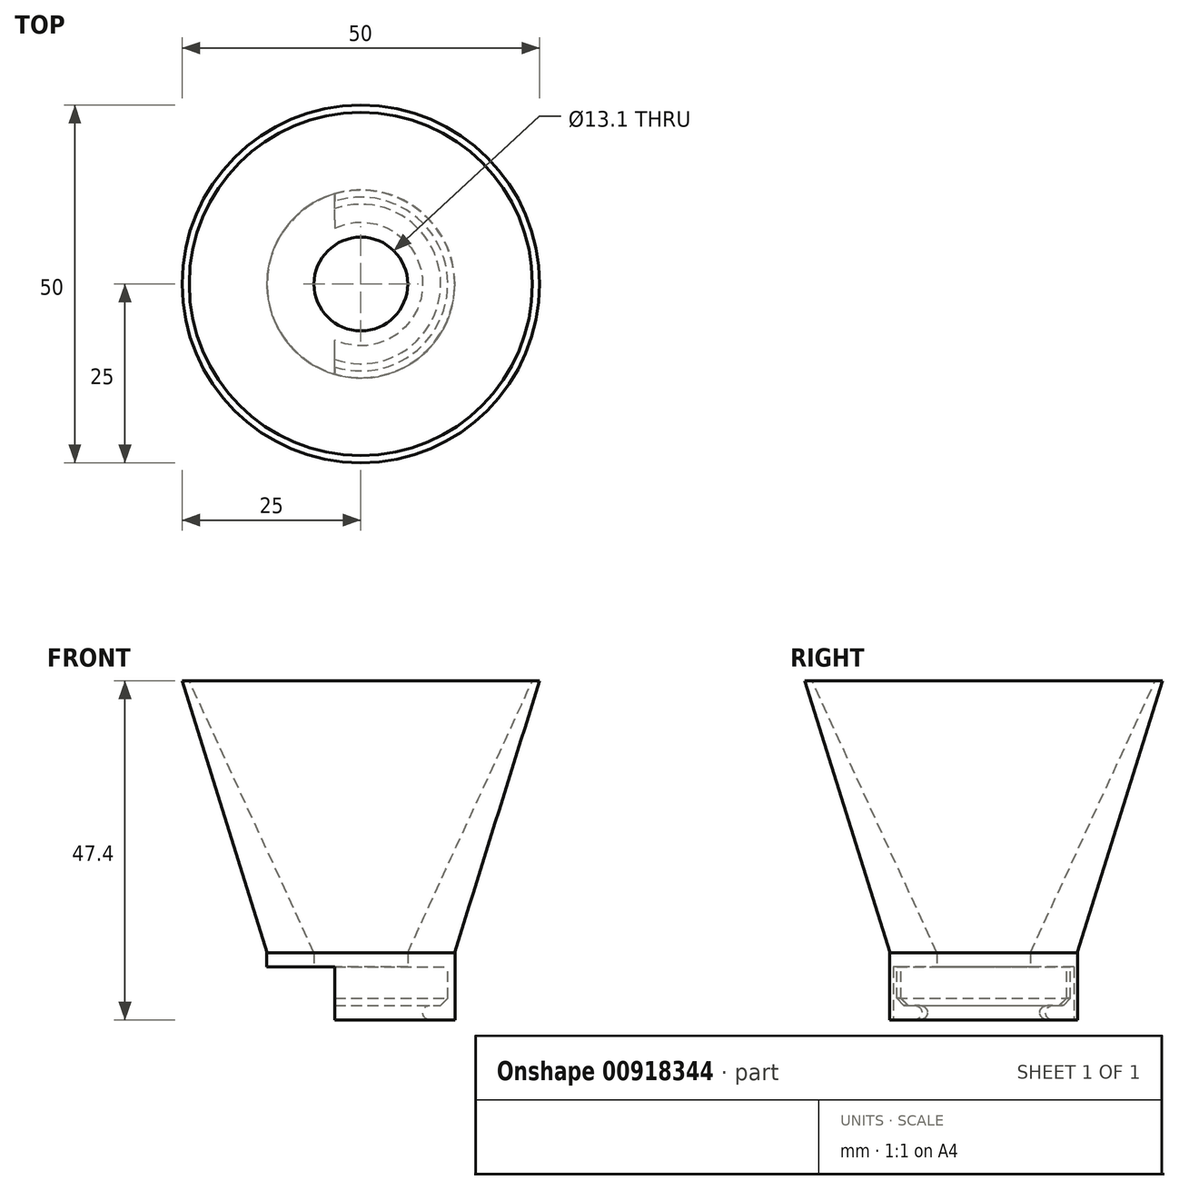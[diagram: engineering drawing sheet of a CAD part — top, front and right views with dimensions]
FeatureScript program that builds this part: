
annotation { "Feature Type Name" : "Feature", "Feature Type Description" : "" }
export const myFeature = defineFeature(function(context is Context, id is Id, definition is map)
    precondition{}
    {
        {
            var Q0;
            Q0=qCreatedBy(makeId("Top.planeOp"),FACE);
            var sketch = newSketch(context, id + "F0", { "sketchPlane" : qUnion([Q0])});
            skCircle(sketch, "E0", {"center": v(0, 0) * mm, "radius": 8.65 * mm});
            skCircle(sketch, "E1.0", {"center": v(0, 0) * mm, "radius": 13.15 * mm});
            skLineSegment(sketch, "E2", {"start": v(-3.65, 15.06) * mm, "end": v(-3.65, -15.06) * mm});
            skSolve(sketch);
        }
        {
            var Q0;
            Q0=qCreatedBy(makeId("Top.planeOp"),FACE);
            cPlane(context, id + "F1", {"entities" : qUnion([Q0]), "cplaneType" : CPlaneType.OFFSET, "offset" : 5.4 * mm, "width" : 150 * mm, "height" : 150 * mm});
        }
        {
            var Q0;
            Q0=makeQuery(id+"F0.imprint","IMPRINT",FACE,{"disambiguationData":[TD([[makeQuery(id+"F0.imprint","IMPRINT",EDGE,{"derivedFrom":sQuery(id+"F0.wireOp",EDGE,"E0")}),-1.0]])]});
            extrude(context, id + "F2", {"entities" : qUnion([Q0]), "oppositeDirection" : true, "depth" : 2 * mm, "offsetDistance" : 25 * mm});
        }
        {
            var Q0;
            Q0=qCreatedBy(id+"F1.planeOp",FACE);
            var sketch = newSketch(context, id + "F3", { "sketchPlane" : qUnion([Q0])});
            skCircle(sketch, "E3", {"center": v(0, 0) * mm, "radius": 6.55 * mm});
            skCircle(sketch, "E4.0", {"center": v(0, 0) * mm, "radius": 12.15 * mm});
            skCircle(sketch, "E5.0", {"center": v(0, 0) * mm, "radius": 13.15 * mm});
            skSolve(sketch);
        }
        {
            var Q0;
            Q0=makeQuery(id+"F3.imprint","IMPRINT",FACE,{"disambiguationData":[TD([[makeQuery(id+"F3.imprint","IMPRINT",EDGE,{"derivedFrom":sQuery(id+"F3.wireOp",EDGE,"E3")}),-1.0]])]});
            extrude(context, id + "F4", {"entities" : qUnion([Q0]), "depth" : 2 * mm, "offsetDistance" : 25 * mm});
        }
        {
            var Q0;
            Q0=makeQuery(id+"F3.imprint","IMPRINT",FACE,{"disambiguationData":[TD([[makeQuery(id+"F3.imprint","IMPRINT",EDGE,{"derivedFrom":sQuery(id+"F3.wireOp",EDGE,"E4.0")}),-1.0]])]});
            extrude(context, id + "F5", {"entities" : qUnion([Q0]), "operationType" : NewBodyOperationType.ADD, "oppositeDirection" : true, "depth" : 6.2 * mm, "offsetDistance" : 25 * mm, "hasSecondDirection" : true, "secondDirectionOppositeDirection" : false, "secondDirectionDepth" : 2 * mm});
        }
        {
            var Q0;
            {var subQ0=sQuery(id+"F0.wireOp",EDGE,"E2");var subQ1=sQuery(id+"F0.wireOp",EDGE,"E0");var subQ2=makeQuery(id+"F0.imprint","INTERSECT",VERTEX,{"disambiguationData":[OD(0.0)],"derivedFrom":[subQ1,subQ0]});Q0=makeQuery(id+"F0.imprint","IMPRINT",FACE,{"disambiguationData":[TD([[makeQuery(id+"F0.imprint","IMPRINT",EDGE,{"disambiguationData":[TD([[subQ2,-1.0]])],"derivedFrom":subQ1}),-1.0]])]});}
            extrude(context, id + "F6", {"entities" : qUnion([Q0]), "operationType" : NewBodyOperationType.REMOVE, "depth" : 5.4 * mm, "offsetDistance" : 25 * mm, "hasSecondDirection" : true, "secondDirectionOppositeDirection" : true, "secondDirectionDepth" : 25 * mm});
        }
        {
            var Q0;
            Q0=makeQuery(id+"F5.boolean.opBoolean","INTERSECT",EDGE,{"derivedFrom":[makeQuery(id+"F2.opExtrude","CAP_FACE",FACE,{"disambiguationData":[OSD([sQuery(id+"F0.wireOp",EDGE,"E0"),sQuery(id+"F0.wireOp",EDGE,"E1.0")])],"isStart":true}),makeQuery(id+"F5.opExtrude","SWEPT_FACE",FACE,{"disambiguationData":[OSD([sQuery(id+"F3.wireOp",EDGE,"E4.0")])]})]});
            chamfer(context, id + "F7", {"entities" : qUnion([Q0]), "width" : 1 * mm, "tangentPropagation" : true});
        }
        {
            var Q0;
            Q0=makeQuery(id+"F2.opExtrude","CAP_EDGE",EDGE,{"disambiguationData":[OSD([sQuery(id+"F0.wireOp",EDGE,"E0")])],"isStart":true});
            var Q1;
            Q1=makeQuery(id+"F2.opExtrude","CAP_EDGE",EDGE,{"disambiguationData":[OSD([sQuery(id+"F0.wireOp",EDGE,"E0")])],"isStart":false});
            fillet(context, id + "F8", {"entities" : qUnion([Q0, Q1]), "radius" : 1 * mm, "tangentPropagation" : true, "allowEdgeOverflow" : false});
        }
        {
            var Q0;
            Q0=qCreatedBy(id+"F1.planeOp",FACE);
            cPlane(context, id + "F9", {"entities" : qUnion([Q0]), "cplaneType" : CPlaneType.OFFSET, "offset" : 40 * mm, "width" : 150 * mm, "height" : 150 * mm});
        }
        {
            var Q0;
            Q0=qCreatedBy(id+"F9.planeOp",FACE);
            var sketch = newSketch(context, id + "F10", { "sketchPlane" : qUnion([Q0])});
            skCircle(sketch, "E6", {"center": v(0, 0) * mm, "radius": 25 * mm});
            skSolve(sketch);
        }
        {
            var Q0;
            {var subQ0=sQuery(id+"F3.wireOp",EDGE,"E4.0");Q0=makeQuery(id+"F5.boolean.opBoolean","MERGE",FACE,{"derivedFrom":[makeQuery(id+"F4.opExtrude","CAP_FACE",FACE,{"disambiguationData":[OSD([sQuery(id+"F3.wireOp",EDGE,"E3"),subQ0])],"isStart":false}),makeQuery(id+"F5.opExtrude","CAP_FACE",FACE,{"disambiguationData":[OSD([subQ0,sQuery(id+"F3.wireOp",EDGE,"E5.0")])],"isStart":true})]});}
            var sketch = newSketch(context, id + "F11", { "sketchPlane" : qUnion([Q0])});
            skCircle(sketch, "E7", {"center": v(0, 0) * mm, "radius": 13.1 * mm});
            skSolve(sketch);
        }
        {
            var Q1;
            Q1 = qSketchRegion(id + "F11", true);
            var Q2;
            Q2=makeQuery(id+"F10.imprint","IMPRINT",FACE,{"disambiguationData":[TD([[makeQuery(id+"F10.imprint","IMPRINT",EDGE,{"derivedFrom":sQuery(id+"F10.wireOp",EDGE,"E6")}),1.0]])]});
            loft(context, id + "F12", {"sheetProfilesArray" : [{ "sheetProfileEntities" : qUnion([Q1]) }, { "sheetProfileEntities" : qUnion([Q2]) }]});
        }
        {
            var Q0;
            Q0=makeQuery(id+"F12.opLoft","CAP_FACE",FACE,{"disambiguationData":[OSD([makeQuery(id+"F10.imprint","IMPRINT",FACE,{"disambiguationData":[TD([[makeQuery(id+"F10.imprint","IMPRINT",EDGE,{"derivedFrom":sQuery(id+"F10.wireOp",EDGE,"E6")}),1.0]])]})])],"isStart":true});
            var sketch = newSketch(context, id + "F13", { "sketchPlane" : qUnion([Q0])});
            skCircle(sketch, "E8", {"center": v(0, 0) * mm, "radius": 24 * mm});
            skSolve(sketch);
        }
        {
            var Q0;
            {var subQ0=sQuery(id+"F3.wireOp",EDGE,"E4.0");Q0=makeQuery(id+"F5.boolean.opBoolean","MERGE",FACE,{"derivedFrom":[makeQuery(id+"F4.opExtrude","CAP_FACE",FACE,{"disambiguationData":[OSD([sQuery(id+"F3.wireOp",EDGE,"E3"),subQ0])],"isStart":false}),makeQuery(id+"F5.opExtrude","CAP_FACE",FACE,{"disambiguationData":[OSD([subQ0,sQuery(id+"F3.wireOp",EDGE,"E5.0")])],"isStart":true})]});}
            var sketch = newSketch(context, id + "F14", { "sketchPlane" : qUnion([Q0])});
            skCircle(sketch, "E9", {"center": v(0, 0) * mm, "radius": 6.55 * mm});
            skSolve(sketch);
        }
        {
            var Q1;
            Q1=makeQuery(id+"F13.imprint","IMPRINT",FACE,{"disambiguationData":[TD([[makeQuery(id+"F13.imprint","IMPRINT",EDGE,{"derivedFrom":sQuery(id+"F13.wireOp",EDGE,"E8")}),1.0]])]});
            var Q2;
            Q2=makeQuery(id+"F14.imprint","IMPRINT",FACE,{"disambiguationData":[TD([[makeQuery(id+"F14.imprint","IMPRINT",EDGE,{"derivedFrom":sQuery(id+"F14.wireOp",EDGE,"E9")}),1.0]])]});
            loft(context, id + "F15", {"operationType" : NewBodyOperationType.REMOVE, "sheetProfilesArray" : [{ "sheetProfileEntities" : qUnion([Q1]) }, { "sheetProfileEntities" : qUnion([Q2]) }]});
        }
    });
